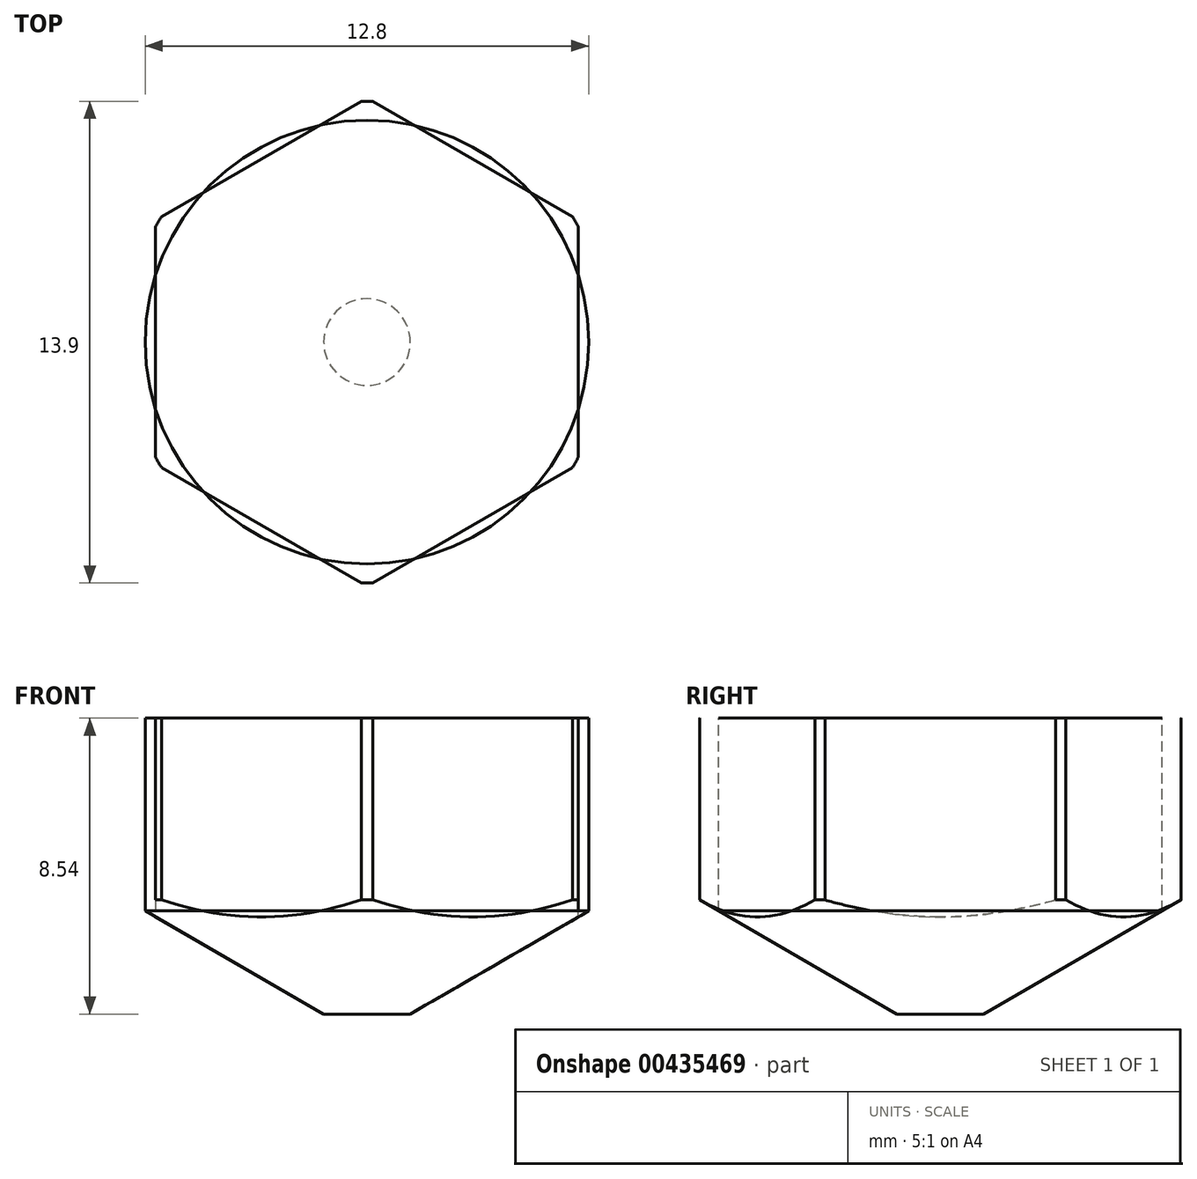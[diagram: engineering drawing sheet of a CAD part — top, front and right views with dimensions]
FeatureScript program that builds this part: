
annotation { "Feature Type Name" : "Feature", "Feature Type Description" : "" }
export const myFeature = defineFeature(function(context is Context, id is Id, definition is map)
    precondition{}
    {
        {
            var Q0;
            Q0=qCreatedBy(makeId("Front.planeOp"),FACE);
            var sketch = newSketch(context, id + "F0", { "sketchPlane" : qUnion([Q0])});
            skLineSegment(sketch, "E0", {"start": v(0, 0) * mm, "end": v(1.25, 0) * mm});
            skLineSegment(sketch, "E1", {"start": v(1.25, 0) * mm, "end": v(6.95, 3.3) * mm});
            skLineSegment(sketch, "E2", {"start": v(6.95, 3.3) * mm, "end": v(6.95, 8.54) * mm});
            skLineSegment(sketch, "E3", {"start": v(6.95, 8.54) * mm, "end": v(0, 8.54) * mm});
            skLineSegment(sketch, "E4", {"start": v(0, 8.54) * mm, "end": v(0, 0) * mm});
            skLineSegment(sketch, "E5", {"start": v(0, 8.54) * mm, "end": v(0, 0) * mm, "construction": true});
            skSolve(sketch);
        }
        {
            var Q0;
            Q0 = qSketchRegion(id + "F0", true);
            var Q1;
            Q1=sQuery(id+"F0.wireOp",EDGE,"E4");
            revolve(context, id + "F1", {"surfaceOperationType" : NewSurfaceOperationType.NEW, "entities" : qUnion([Q0]), "axis" : qUnion([Q1]), "revolveType" : RevolveType.FULL});
        }
        {
            var Q0;
            Q0=makeQuery(id+"F1.opRevolve","SWEPT_FACE",FACE,{"disambiguationData":[OSD([sQuery(id+"F0.wireOp",EDGE,"E3")])]});
            var sketch = newSketch(context, id + "F2", { "sketchPlane" : qUnion([Q0])});
            skCircle(sketch, "E6.cCircle", {"center": v(0, 0) * mm, "radius": 6.1 * mm, "construction": true});
            skLineSegment(sketch, "E6.0", {"start": v(6.1, 3.52) * mm, "end": v(6.1, -3.52) * mm});
            skLineSegment(sketch, "E6.1", {"start": v(6.1, -3.52) * mm, "end": v(0, -7.04) * mm});
            skLineSegment(sketch, "E6.2", {"start": v(0, -7.04) * mm, "end": v(-6.1, -3.52) * mm});
            skLineSegment(sketch, "E6.3", {"start": v(-6.1, -3.52) * mm, "end": v(-6.1, 3.52) * mm});
            skLineSegment(sketch, "E6.4", {"start": v(-6.1, 3.52) * mm, "end": v(0, 7.04) * mm});
            skLineSegment(sketch, "E6.5", {"start": v(0, 7.04) * mm, "end": v(6.1, 3.52) * mm});
            skPoint(sketch, "E6.0.midPoint", {"position": v(6.1, 0) * mm});
            skCircle(sketch, "E7", {"center": v(0, 0) * mm, "radius": 10.5 * mm});
            skSolve(sketch);
        }
        {
            var Q0;
            Q0 = qSketchRegion(id + "F2", true);
            extrude(context, id + "F3", {"entities" : qUnion([Q0]), "operationType" : NewBodyOperationType.REMOVE, "oppositeDirection" : true, "depth" : 25 * mm, "offsetDistance" : 25 * mm});
        }
        {
            var Q0;
            Q0=qCreatedBy(makeId("Front.planeOp"),FACE);
            var sketch = newSketch(context, id + "F4", { "sketchPlane" : qUnion([Q0])});
            skLineSegment(sketch, "E8", {"start": v(0, 0) * mm, "end": v(1.25, 0) * mm});
            skLineSegment(sketch, "E9", {"start": v(1.25, 0) * mm, "end": v(6.4, 2.97) * mm});
            skLineSegment(sketch, "E10", {"start": v(6.4, 2.97) * mm, "end": v(6.4, 8.54) * mm});
            skLineSegment(sketch, "E11", {"start": v(6.4, 8.54) * mm, "end": v(0, 8.54) * mm});
            skLineSegment(sketch, "E12", {"start": v(0, 8.54) * mm, "end": v(0, 0) * mm});
            skLineSegment(sketch, "E13", {"start": v(0, 8.54) * mm, "end": v(0, 0) * mm, "construction": true});
            skSolve(sketch);
        }
        {
            var Q0;
            Q0 = qSketchRegion(id + "F4", true);
            var Q1;
            Q1=sQuery(id+"F4.wireOp",EDGE,"E12");
            revolve(context, id + "F5", {"surfaceOperationType" : NewSurfaceOperationType.NEW, "entities" : qUnion([Q0]), "axis" : qUnion([Q1]), "revolveType" : RevolveType.FULL});
        }
    });
